annotation { "Feature Type Name" : "Feature", "Feature Type Description" : "" }
export const myFeature = defineFeature(function(context is Context, id is Id, definition is map)
    precondition{}
    {
        {
            var Q0;
            Q0=qCreatedBy(makeId("Top.planeOp"),FACE);
            var sketch = newSketch(context, id + "F0", { "sketchPlane" : qUnion([Q0])});
            skLineSegment(sketch, "E0.bottom", {"start": v(0, -29.35) * mm, "end": v(63.5, -29.35) * mm});
            skLineSegment(sketch, "E0.top", {"start": v(0, -48.4) * mm, "end": v(63.5, -48.4) * mm});
            skLineSegment(sketch, "E0.left", {"start": v(0, -29.35) * mm, "end": v(0, -48.4) * mm});
            skLineSegment(sketch, "E0.right", {"start": v(63.5, -29.35) * mm, "end": v(63.5, -48.4) * mm});
            skSolve(sketch);
        }
        {
            var Q0;
            Q0=makeQuery(id+"F0.imprint","IMPRINT",FACE,{"disambiguationData":[TD([[makeQuery(id+"F0.imprint","IMPRINT",EDGE,{"derivedFrom":sQuery(id+"F0.wireOp",EDGE,"E0.bottom")}),-1.0]])]});
            extrude(context, id + "F1", {"entities" : qUnion([Q0]), "depth" : 3.8 * mm, "offsetDistance" : 25.4 * mm});
        }
        {
            var Q0;
            Q0=makeQuery(id+"F1.opExtrude","CAP_FACE",FACE,{"disambiguationData":[OSD([sQuery(id+"F0.wireOp",EDGE,"E0.bottom"),sQuery(id+"F0.wireOp",EDGE,"E0.top"),sQuery(id+"F0.wireOp",EDGE,"E0.left"),sQuery(id+"F0.wireOp",EDGE,"E0.right")])],"isStart":false});
            var sketch = newSketch(context, id + "F2", { "sketchPlane" : qUnion([Q0])});
            skArc(sketch, "E1", {"start": v(8.65, -32.74) * mm, "mid": v(8.04, -32.85) * mm, "end": v(7.45, -33.02) * mm});
            skArc(sketch, "E2", {"start": v(7.45, -33.02) * mm, "mid": v(6.94, -33.23) * mm, "end": v(6.43, -33.46) * mm});
            skArc(sketch, "E3", {"start": v(6.43, -33.46) * mm, "mid": v(5.96, -33.73) * mm, "end": v(5.53, -34.05) * mm});
            skArc(sketch, "E4", {"start": v(5.53, -34.05) * mm, "mid": v(5.19, -34.32) * mm, "end": v(4.87, -34.6) * mm});
            skArc(sketch, "E5", {"start": v(4.87, -34.6) * mm, "mid": v(4.5, -34.96) * mm, "end": v(4.19, -35.34) * mm});
            skArc(sketch, "E6", {"start": v(4.19, -35.34) * mm, "mid": v(3.94, -35.7) * mm, "end": v(3.73, -36.06) * mm});
            skArc(sketch, "E7", {"start": v(3.73, -36.06) * mm, "mid": v(3.53, -36.48) * mm, "end": v(3.38, -36.92) * mm});
            skArc(sketch, "E8", {"start": v(3.38, -36.92) * mm, "mid": v(3.3, -37.23) * mm, "end": v(3.24, -37.55) * mm});
            skArc(sketch, "E9", {"start": v(3.24, -37.55) * mm, "mid": v(3.22, -38.06) * mm, "end": v(3.24, -38.57) * mm});
            skArc(sketch, "E10", {"start": v(3.24, -38.57) * mm, "mid": v(3.29, -38.87) * mm, "end": v(3.34, -39.16) * mm});
            skArc(sketch, "E11", {"start": v(3.34, -39.16) * mm, "mid": v(3.4, -39.38) * mm, "end": v(3.47, -39.6) * mm});
            skArc(sketch, "E12", {"start": v(3.47, -39.6) * mm, "mid": v(3.6, -39.9) * mm, "end": v(3.73, -40.18) * mm});
            skArc(sketch, "E13", {"start": v(3.73, -40.18) * mm, "mid": v(3.89, -40.47) * mm, "end": v(4.07, -40.74) * mm});
            skArc(sketch, "E14", {"start": v(4.07, -40.74) * mm, "mid": v(4.22, -40.93) * mm, "end": v(4.37, -41.12) * mm});
            skArc(sketch, "E15", {"start": v(4.37, -41.12) * mm, "mid": v(4.47, -41.25) * mm, "end": v(4.59, -41.36) * mm});
            skArc(sketch, "E16", {"start": v(4.59, -41.36) * mm, "mid": v(4.75, -41.53) * mm, "end": v(4.92, -41.69) * mm});
            skArc(sketch, "E17", {"start": v(4.92, -41.69) * mm, "mid": v(5.09, -41.82) * mm, "end": v(5.25, -41.94) * mm});
            skArc(sketch, "E18", {"start": v(5.25, -41.94) * mm, "mid": v(5.37, -42.03) * mm, "end": v(5.49, -42.11) * mm});
            skArc(sketch, "E19", {"start": v(5.49, -42.11) * mm, "mid": v(5.62, -42.2) * mm, "end": v(5.76, -42.3) * mm});
            skArc(sketch, "E20", {"start": v(5.76, -42.3) * mm, "mid": v(5.87, -42.36) * mm, "end": v(6, -42.43) * mm});
            skArc(sketch, "E21", {"start": v(6, -42.43) * mm, "mid": v(6.22, -42.55) * mm, "end": v(6.45, -42.65) * mm});
            skArc(sketch, "E22", {"start": v(6.45, -42.65) * mm, "mid": v(6.72, -42.76) * mm, "end": v(6.98, -42.86) * mm});
            skArc(sketch, "E23", {"start": v(6.98, -42.86) * mm, "mid": v(7.29, -42.96) * mm, "end": v(7.6, -43.04) * mm});
            skArc(sketch, "E24", {"start": v(7.6, -43.04) * mm, "mid": v(7.88, -43.1) * mm, "end": v(8.17, -43.14) * mm});
            skArc(sketch, "E25", {"start": v(8.17, -43.14) * mm, "mid": v(8.45, -43.18) * mm, "end": v(8.74, -43.2) * mm});
            skArc(sketch, "E26", {"start": v(8.74, -43.2) * mm, "mid": v(9.24, -43.23) * mm, "end": v(9.75, -43.22) * mm});
            skArc(sketch, "E27", {"start": v(9.75, -43.22) * mm, "mid": v(10.22, -43.19) * mm, "end": v(10.69, -43.14) * mm});
            skArc(sketch, "E28", {"start": v(10.69, -43.14) * mm, "mid": v(11.1, -43.07) * mm, "end": v(11.5, -42.98) * mm});
            skArc(sketch, "E29", {"start": v(11.5, -42.98) * mm, "mid": v(11.77, -42.91) * mm, "end": v(12.04, -42.84) * mm});
            skArc(sketch, "E30", {"start": v(12.04, -42.84) * mm, "mid": v(12.52, -42.69) * mm, "end": v(12.99, -42.52) * mm});
            skArc(sketch, "E31", {"start": v(12.99, -42.52) * mm, "mid": v(13.2, -42.44) * mm, "end": v(13.4, -42.34) * mm});
            skLineSegment(sketch, "E32", {"start": v(13.4, -42.34) * mm, "end": v(13.4, -42.64) * mm});
            skLineSegment(sketch, "E33", {"start": v(13.4, -42.64) * mm, "end": v(15.62, -42.64) * mm});
            skLineSegment(sketch, "E34", {"start": v(15.62, -42.64) * mm, "end": v(15.62, -38.98) * mm});
            skLineSegment(sketch, "E35", {"start": v(15.62, -38.98) * mm, "end": v(16.23, -38.98) * mm});
            skLineSegment(sketch, "E36", {"start": v(16.23, -38.98) * mm, "end": v(16.23, -43.04) * mm});
            skLineSegment(sketch, "E37", {"start": v(16.23, -43.04) * mm, "end": v(15.06, -43.04) * mm});
            skLineSegment(sketch, "E38", {"start": v(15.06, -43.04) * mm, "end": v(15.06, -45.2) * mm});
            skLineSegment(sketch, "E39", {"start": v(15.06, -45.2) * mm, "end": v(20.1, -45.2) * mm});
            skLineSegment(sketch, "E40", {"start": v(20.1, -45.2) * mm, "end": v(20.1, -43.03) * mm});
            skLineSegment(sketch, "E41", {"start": v(20.1, -43.03) * mm, "end": v(18.99, -43.03) * mm});
            skLineSegment(sketch, "E42", {"start": v(18.99, -43.03) * mm, "end": v(18.99, -38.97) * mm});
            skLineSegment(sketch, "E43", {"start": v(18.99, -38.97) * mm, "end": v(21.3, -38.97) * mm});
            skLineSegment(sketch, "E44", {"start": v(21.3, -38.97) * mm, "end": v(21.48, -39.92) * mm});
            skLineSegment(sketch, "E45", {"start": v(21.48, -39.92) * mm, "end": v(23.37, -39.92) * mm});
            skLineSegment(sketch, "E46", {"start": v(23.37, -39.92) * mm, "end": v(23.37, -36.63) * mm});
            skLineSegment(sketch, "E47", {"start": v(23.37, -36.63) * mm, "end": v(11.12, -36.63) * mm});
            skLineSegment(sketch, "E48", {"start": v(11.12, -36.63) * mm, "end": v(11.12, -39.9) * mm});
            skLineSegment(sketch, "E49", {"start": v(11.12, -39.9) * mm, "end": v(13, -39.9) * mm});
            skLineSegment(sketch, "E50", {"start": v(13, -39.9) * mm, "end": v(13.18, -38.98) * mm});
            skLineSegment(sketch, "E51", {"start": v(13.18, -38.98) * mm, "end": v(13.69, -38.98) * mm});
            skArc(sketch, "E52", {"start": v(13.42, -39.62) * mm, "mid": v(13.57, -39.3) * mm, "end": v(13.69, -38.98) * mm});
            skArc(sketch, "E53", {"start": v(13.16, -40.01) * mm, "mid": v(13.3, -39.82) * mm, "end": v(13.42, -39.62) * mm});
            skArc(sketch, "E54", {"start": v(12.86, -40.33) * mm, "mid": v(13.02, -40.18) * mm, "end": v(13.16, -40.01) * mm});
            skArc(sketch, "E55", {"start": v(12.5, -40.6) * mm, "mid": v(12.69, -40.47) * mm, "end": v(12.86, -40.33) * mm});
            skArc(sketch, "E56", {"start": v(11.98, -40.88) * mm, "mid": v(12.24, -40.75) * mm, "end": v(12.5, -40.6) * mm});
            skArc(sketch, "E57", {"start": v(11.51, -41.04) * mm, "mid": v(11.75, -40.97) * mm, "end": v(11.98, -40.88) * mm});
            skArc(sketch, "E58", {"start": v(10.79, -41.17) * mm, "mid": v(11.15, -41.12) * mm, "end": v(11.51, -41.04) * mm});
            skArc(sketch, "E59", {"start": v(9.25, -41.1) * mm, "mid": v(10.02, -41.17) * mm, "end": v(10.79, -41.17) * mm});
            skArc(sketch, "E60", {"start": v(8.51, -40.85) * mm, "mid": v(8.88, -41) * mm, "end": v(9.25, -41.1) * mm});
            skArc(sketch, "E61", {"start": v(7.91, -40.57) * mm, "mid": v(8.2, -40.72) * mm, "end": v(8.51, -40.85) * mm});
            skArc(sketch, "E62", {"start": v(7.34, -40.14) * mm, "mid": v(7.61, -40.37) * mm, "end": v(7.91, -40.57) * mm});
            skArc(sketch, "E63", {"start": v(6.9, -39.65) * mm, "mid": v(7.1, -39.9) * mm, "end": v(7.34, -40.14) * mm});
            skArc(sketch, "E64", {"start": v(6.58, -39.01) * mm, "mid": v(6.72, -39.34) * mm, "end": v(6.9, -39.65) * mm});
            skArc(sketch, "E65", {"start": v(6.52, -38.86) * mm, "mid": v(6.55, -38.94) * mm, "end": v(6.58, -39) * mm});
            skArc(sketch, "E66", {"start": v(6.5, -37.6) * mm, "mid": v(6.44, -38.23) * mm, "end": v(6.52, -38.86) * mm});
            skArc(sketch, "E67", {"start": v(6.73, -36.92) * mm, "mid": v(6.59, -37.25) * mm, "end": v(6.5, -37.6) * mm});
            skArc(sketch, "E68", {"start": v(7.12, -36.32) * mm, "mid": v(6.91, -36.61) * mm, "end": v(6.73, -36.92) * mm});
            skArc(sketch, "E69", {"start": v(7.76, -35.73) * mm, "mid": v(7.43, -36) * mm, "end": v(7.12, -36.32) * mm});
            skArc(sketch, "E70", {"start": v(8.51, -35.3) * mm, "mid": v(8.12, -35.49) * mm, "end": v(7.76, -35.73) * mm});
            skArc(sketch, "E71", {"start": v(9.29, -35.07) * mm, "mid": v(8.9, -35.16) * mm, "end": v(8.51, -35.3) * mm});
            skArc(sketch, "E72", {"start": v(10, -34.98) * mm, "mid": v(9.64, -35) * mm, "end": v(9.29, -35.07) * mm});
            skArc(sketch, "E73", {"start": v(10.79, -35.01) * mm, "mid": v(10.4, -34.99) * mm, "end": v(10, -34.98) * mm});
            skArc(sketch, "E74", {"start": v(11.47, -35.17) * mm, "mid": v(11.13, -35.07) * mm, "end": v(10.79, -35.01) * mm});
            skArc(sketch, "E75", {"start": v(12.1, -35.42) * mm, "mid": v(11.8, -35.27) * mm, "end": v(11.47, -35.17) * mm});
            skArc(sketch, "E76", {"start": v(12.71, -35.73) * mm, "mid": v(12.41, -35.57) * mm, "end": v(12.1, -35.42) * mm});
            skArc(sketch, "E77", {"start": v(13.16, -36.03) * mm, "mid": v(12.94, -35.87) * mm, "end": v(12.71, -35.73) * mm});
            skArc(sketch, "E78", {"start": v(13.42, -36.25) * mm, "mid": v(13.3, -36.14) * mm, "end": v(13.16, -36.03) * mm});
            skLineSegment(sketch, "E79", {"start": v(13.42, -36.25) * mm, "end": v(15.46, -36.25) * mm});
            skLineSegment(sketch, "E80", {"start": v(15.46, -36.25) * mm, "end": v(15.46, -32.66) * mm});
            skLineSegment(sketch, "E81", {"start": v(15.46, -32.66) * mm, "end": v(13.36, -32.66) * mm});
            skLineSegment(sketch, "E82", {"start": v(13.36, -32.66) * mm, "end": v(13.36, -33.66) * mm});
            skArc(sketch, "E83", {"start": v(13.36, -33.66) * mm, "mid": v(12.9, -33.41) * mm, "end": v(12.4, -33.23) * mm});
            skArc(sketch, "E84", {"start": v(12.4, -33.23) * mm, "mid": v(11.98, -33.06) * mm, "end": v(11.53, -32.93) * mm});
            skArc(sketch, "E85", {"start": v(11.53, -32.93) * mm, "mid": v(11.09, -32.81) * mm, "end": v(10.62, -32.76) * mm});
            skArc(sketch, "E86", {"start": v(10.62, -32.76) * mm, "mid": v(10.13, -32.69) * mm, "end": v(9.63, -32.68) * mm});
            skArc(sketch, "E87", {"start": v(9.63, -32.68) * mm, "mid": v(9.13, -32.68) * mm, "end": v(8.65, -32.74) * mm});
            skLineSegment(sketch, "E88", {"start": v(6.58, -39) * mm, "end": v(6.58, -39.01) * mm});
            skSolve(sketch);
        }
        {
            var Q0;
            Q0=makeQuery(id+"F2.imprint","IMPRINT",FACE,{"disambiguationData":[TD([[makeQuery(id+"F2.imprint","IMPRINT",EDGE,{"derivedFrom":sQuery(id+"F2.wireOp",EDGE,"E1")}),1.0]])]});
            extrude(context, id + "F3", {"entities" : qUnion([Q0]), "operationType" : NewBodyOperationType.REMOVE, "oppositeDirection" : true, "depth" : 3.8 * mm, "offsetDistance" : 25.4 * mm});
        }
        {
            var Q0;
            Q0=makeQuery(id+"F1.opExtrude","SWEPT_EDGE",EDGE,{"disambiguationData":[OSD([sQuery(id+"F0.wireOp",EDGE,"E0.top"),sQuery(id+"F0.wireOp",EDGE,"E0.right")])]});
            chamfer(context, id + "F4", {"entities" : qUnion([Q0]), "width" : 5.08 * mm, "tangentPropagation" : true});
        }
        {
            var Q0;
            Q0=makeQuery(id+"F1.opExtrude","SWEPT_EDGE",EDGE,{"disambiguationData":[OSD([sQuery(id+"F0.wireOp",EDGE,"E0.bottom"),sQuery(id+"F0.wireOp",EDGE,"E0.right")])]});
            chamfer(context, id + "F5", {"entities" : qUnion([Q0]), "width" : 5.08 * mm, "tangentPropagation" : true});
        }
        {
            var Q0;
            Q0=makeQuery(id+"F1.opExtrude","SWEPT_EDGE",EDGE,{"disambiguationData":[OSD([sQuery(id+"F0.wireOp",EDGE,"E0.top"),sQuery(id+"F0.wireOp",EDGE,"E0.left")])]});
            fillet(context, id + "F6", {"entities" : qUnion([Q0]), "radius" : 7.62 * mm, "tangentPropagation" : true, "allowEdgeOverflow" : false});
        }
        {
            var Q0;
            Q0=makeQuery(id+"F1.opExtrude","SWEPT_EDGE",EDGE,{"disambiguationData":[OSD([sQuery(id+"F0.wireOp",EDGE,"E0.bottom"),sQuery(id+"F0.wireOp",EDGE,"E0.left")])]});
            fillet(context, id + "F7", {"entities" : qUnion([Q0]), "radius" : 7.62 * mm, "tangentPropagation" : true, "allowEdgeOverflow" : false});
        }
        {
            var Q0;
            Q0=makeQuery(id+"F1.opExtrude","CAP_FACE",FACE,{"disambiguationData":[OSD([sQuery(id+"F0.wireOp",EDGE,"E0.bottom"),sQuery(id+"F0.wireOp",EDGE,"E0.top"),sQuery(id+"F0.wireOp",EDGE,"E0.left"),sQuery(id+"F0.wireOp",EDGE,"E0.right")])],"isStart":false});
            var sketch = newSketch(context, id + "F8", { "sketchPlane" : qUnion([Q0])});
            skText(sketch, "E89", { "text": "Savannah Hearn", "fontName": "OpenSans-Regular.ttf"});
            const initialGuessF8  = {"E89": [0.02794, -0.0357, 1, 0, 0.00254]};
            skSetInitialGuess(sketch, initialGuessF8);
            skSolve(sketch);
        }
        {
            var Q0;
            Q0=makeQuery(id+"F8.imprint","IMPRINT",FACE,{"disambiguationData":[TD([[makeQuery(id+"F8.imprint","IMPRINT",EDGE,{"derivedFrom":sQuery(id+"F8.wireOp",EDGE,"E89.sketch_text.stroke-0")}),1.0]])]});
            var sketch = newSketch(context, id + "F9", { "sketchPlane" : qUnion([Q0])});
            skText(sketch, "E90", { "text": "GTRI 2017", "fontName": "OpenSans-Regular.ttf"});
            const initialGuessF9  = {"E90": [0.02794, -0.04332, 1, 0, 0.00381]};
            skSetInitialGuess(sketch, initialGuessF9);
            skSolve(sketch);
        }
        {
            var Q0;
            Q0 = qSketchRegion(id + "F8", true);
            extrude(context, id + "F10", {"entities" : qUnion([Q0]), "operationType" : NewBodyOperationType.REMOVE, "oppositeDirection" : true, "depth" : 1.52 * mm, "offsetDistance" : 25.4 * mm});
        }
        {
            var Q0;
            Q0 = qSketchRegion(id + "F9", true);
            extrude(context, id + "F11", {"entities" : qUnion([Q0]), "operationType" : NewBodyOperationType.REMOVE, "oppositeDirection" : true, "depth" : 1.52 * mm, "offsetDistance" : 25.4 * mm});
        }
        {
            var Q0;
            Q0=makeQuery(id+"F1.opExtrude","SWEPT_FACE",FACE,{"disambiguationData":[OSD([sQuery(id+"F0.wireOp",EDGE,"E0.left")])]});
            var sketch = newSketch(context, id + "F12", { "sketchPlane" : qUnion([Q0])});
            skLineSegment(sketch, "E91.bottom", {"start": v(36.97, 0) * mm, "end": v(40.78, 0) * mm});
            skLineSegment(sketch, "E91.top", {"start": v(36.97, 3.81) * mm, "end": v(40.78, 3.81) * mm});
            skLineSegment(sketch, "E91.left", {"start": v(36.97, 0) * mm, "end": v(36.97, 3.81) * mm});
            skLineSegment(sketch, "E91.right", {"start": v(40.78, 0) * mm, "end": v(40.78, 3.81) * mm});
            skSolve(sketch);
        }
        {
            var Q0;
            Q0=makeQuery(id+"F12.imprint","IMPRINT",FACE,{"disambiguationData":[TD([[makeQuery(id+"F12.imprint","IMPRINT",EDGE,{"derivedFrom":sQuery(id+"F12.wireOp",EDGE,"E91.bottom")}),1.0]])]});
            extrude(context, id + "F13", {"entities" : qUnion([Q0]), "operationType" : NewBodyOperationType.ADD, "depth" : 3.56 * mm, "offsetDistance" : 25.4 * mm});
        }
        {
            var Q0;
            {var subQ61=sQuery(id+"F0.wireOp",EDGE,"E0.left");var subQ62=sQuery(id+"F0.wireOp",EDGE,"E0.bottom");var subQ124=sQuery(id+"F0.wireOp",EDGE,"E0.top");var subQ147=sQuery(id+"F0.wireOp",EDGE,"E0.right");var subQ174=makeQuery(id+"F1.opExtrude","SWEPT_FACE",FACE,{"disambiguationData":[OSD([subQ62])]});Q0=makeQuery(id+"F13.boolean.opBoolean","MERGE",FACE,{"derivedFrom":[makeQuery(id+"F11.boolean.opBoolean","SPLIT",FACE,{"disambiguationData":[TD([subQ174])],"derivedFrom":makeQuery(id+"F10.boolean.opBoolean","SPLIT",FACE,{"disambiguationData":[TD([subQ174])],"derivedFrom":makeQuery(id+"F1.opExtrude","CAP_FACE",FACE,{"disambiguationData":[OSD([subQ62,subQ124,subQ61,subQ147])],"isStart":false})})}),makeQuery(id+"F13.opExtrude","SWEPT_FACE",FACE,{"disambiguationData":[OSD([sQuery(id+"F12.wireOp",EDGE,"E91.top")])]})]});}
            var sketch = newSketch(context, id + "F14", { "sketchPlane" : qUnion([Q0])});
            skPoint(sketch, "E92", {"position": v(-1.65, -38.87) * mm});
            skSolve(sketch);
        }
        {
            var Q0;
            Q0=sQuery(id+"F14.wireOp",VERTEX,"E92");
            var Q1;
            Q1=makeQuery(id+"F1.opExtrude","SWEPT_BODY",BODY,{"disambiguationData":[OSD([sQuery(id+"F0.wireOp",EDGE,"E0.bottom"),sQuery(id+"F0.wireOp",EDGE,"E0.top"),sQuery(id+"F0.wireOp",EDGE,"E0.left"),sQuery(id+"F0.wireOp",EDGE,"E0.right")])]});
            hole(context, id + "F15", {"style" : HoleStyle.SIMPLE, "endStyle" : HoleEndStyle.THROUGH, "holeDiameter" : 2.54 * mm, "majorDiameter" : 6.35 * mm, "isTappedThrough" : true, "tappedDepth" : 12.7 * mm, "tapClearance" : 3, "locations" : qUnion([Q0]), "scope" : qUnion([Q1])});
        }
    });